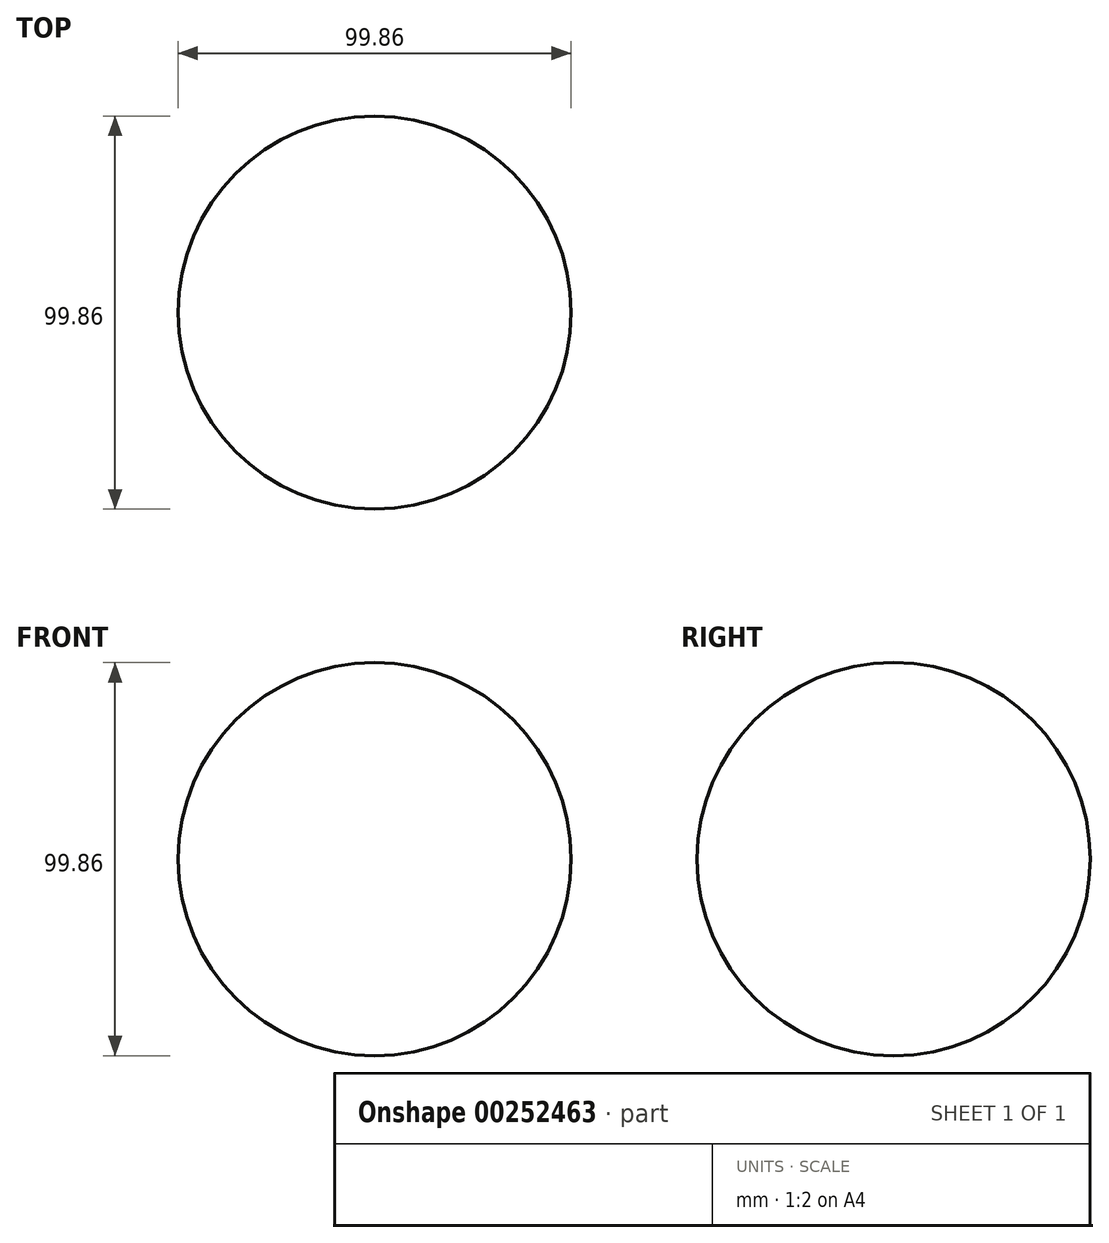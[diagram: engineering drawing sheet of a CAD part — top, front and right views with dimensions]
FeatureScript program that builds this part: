
annotation { "Feature Type Name" : "Feature", "Feature Type Description" : "" }
export const myFeature = defineFeature(function(context is Context, id is Id, definition is map)
    precondition{}
    {
        {
            var Q0;
            Q0=qCreatedBy(makeId("Front.planeOp"),FACE);
            var sketch = newSketch(context, id + "F0", { "sketchPlane" : qUnion([Q0])});
            skArc(sketch, "E0", {"start": v(0, 49.93) * mm, "mid": v(-49.93, 0) * mm, "end": v(0, -49.93) * mm});
            skPoint(sketch, "E1.orphan", {"position": v(0, 123.94) * mm});
            skSolve(sketch);
        }
        {
            var Q0;
            Q0=qCreatedBy(makeId("Front.planeOp"),FACE);
            var sketch = newSketch(context, id + "F1", { "sketchPlane" : qUnion([Q0])});
            skLineSegment(sketch, "E2", {"start": v(0, 117.97) * mm, "end": v(0, -119.57) * mm, "construction": true});
            skSolve(sketch);
        }
        {
            var Q0;
            Q0=sQuery(id+"F0.wireOp",EDGE,"E0");
            var Q1;
            Q1=sQuery(id+"F1.wireOp",EDGE,"E2");
            revolve(context, id + "F2", {"bodyType" : ToolBodyType.SURFACE, "surfaceEntities" : qUnion([Q0]), "axis" : qUnion([Q1]), "revolveType" : RevolveType.FULL});
        }
    });
